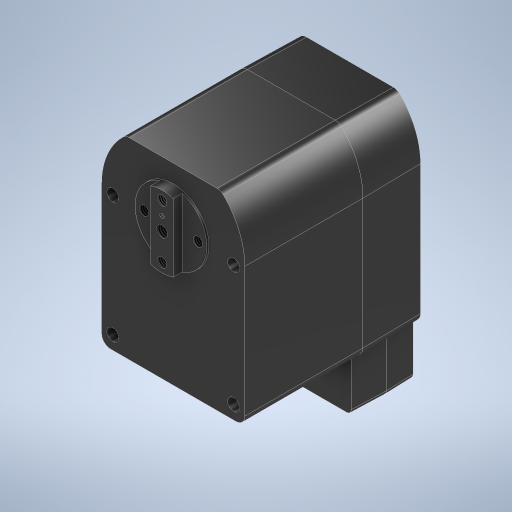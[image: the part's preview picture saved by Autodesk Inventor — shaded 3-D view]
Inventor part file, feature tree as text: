
AUTODESK INVENTOR PART (.ipt)
format: ipt  version: 2024.2 (Build 282272000, 272)  size: 430,080 bytes
history: native  units: mm
features: chamfer x9, hole x7, extrude x6, fillet x2
ambient origin geometry x8: Origin, YZ Plane, XZ Plane, XY Plane, X Axis, Y Axis, Z Axis, Center Point
bodies: Solid1 (feature_tree)
feature tree (24):
  extrude  "Extrusion1"  Depth=16.0mm
  extrude  "Extrusion2"  Depth=16.0mm
  extrude  "Extrusion3"  Depth=43.0mm
  extrude  "Extrusion4"  Depth=9.5mm
  extrude  "Extrusion5"  Depth=32.0mm
  extrude  "Extrusion6"  Depth=28.8mm
  hole  "Hole1"  [1 undecoded]
  hole  "Hole2"  [1 undecoded]
  hole  "Hole3"  [1 undecoded]
  hole  "Hole4"  [1 undecoded]
  hole  "Hole5"  [1 undecoded]
  hole  "Hole6"  [1 undecoded]
  hole  "Hole7"  [1 undecoded]
  chamfer  "Chamfer1"  Distance=12.0mm
  chamfer  "Chamfer2"  Distance=39.5mm
  chamfer  "Chamfer3"  Distance=14.0mm
  chamfer  "Chamfer4"  Distance=0.2mm
  chamfer  "Chamfer5"  Distance=0.5mm
  chamfer  "Chamfer6"  Distance=2.0mm
  chamfer  "Chamfer7"  Distance=13.1mm
  chamfer  "Chamfer8"  Distance=13.1mm
  chamfer  "Chamfer9"  Distance=13.1mm
  fillet  "Fillet1"  Radius=6.1mm
  fillet  "Fillet2"  Radius=6.1mm
note: 7 required parameter values undecoded (feature->parameter linkage not recoverable at this tier; creation-order binding heuristic only, values carry confidence <= 0.55)
